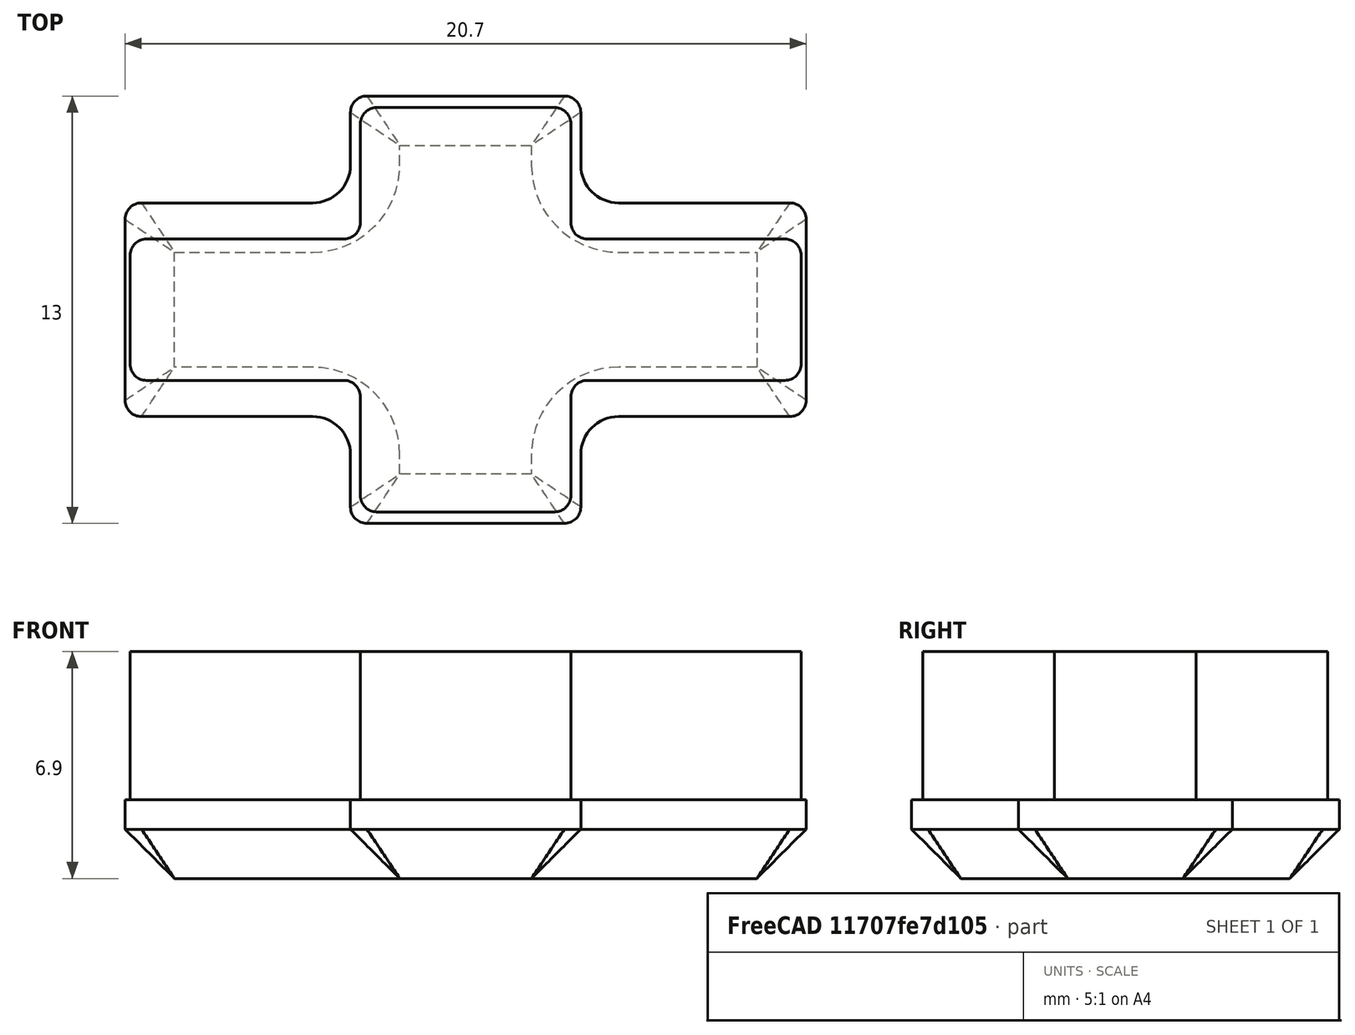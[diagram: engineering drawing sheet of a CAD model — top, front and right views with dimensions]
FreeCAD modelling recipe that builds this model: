
FCSTD DOCUMENT  (FreeCAD 0.19R24366 (Git))
Label: DPAD
License: All rights reserved
LicenseURL: http://en.wikipedia.org/wiki/All_rights_reserved
objects: Sketcher::SketchObject×2, PartDesign::Pad×2, Mesh::Feature×1, PartDesign::Chamfer×1, PartDesign::Body×1
note: 9 computed .brp shape members not serialized (recipe doc carries the construction recipe); baked Part::Feature solids carry a one-line shape summary decoded from their .brp

FEATURE [Sketcher::SketchObject] Sketch
  FullyConstrained = true
  MapMode = 5
  Support = -> [XY_Plane]
  sketch-geometry (24):
    g0: LineSegment StartX=-9.85 StartY=3.25 StartZ=0 EndX=-4.65 EndY=3.25 EndZ=0
    g1: LineSegment StartX=-3.5 StartY=4.4 StartZ=0 EndX=-3.5 EndY=6 EndZ=0
    g2: LineSegment StartX=-3 StartY=6.5 StartZ=0 EndX=3 EndY=6.5 EndZ=0
    g3: LineSegment StartX=3.5 StartY=6 StartZ=0 EndX=3.5 EndY=4.4 EndZ=0
    g4: LineSegment StartX=4.65 StartY=3.25 StartZ=0 EndX=9.85 EndY=3.25 EndZ=0
    g5: LineSegment StartX=10.35 StartY=2.75 StartZ=0 EndX=10.35 EndY=-2.75 EndZ=0
    g6: LineSegment StartX=9.85 StartY=-3.25 StartZ=0 EndX=4.65 EndY=-3.25 EndZ=0
    g7: LineSegment StartX=3.5 StartY=-4.4 StartZ=0 EndX=3.5 EndY=-6 EndZ=0
    g8: LineSegment StartX=3 StartY=-6.5 StartZ=0 EndX=-3 EndY=-6.5 EndZ=0
    g9: LineSegment StartX=-3.5 StartY=-6 StartZ=0 EndX=-3.5 EndY=-4.4 EndZ=0
    g10: LineSegment StartX=-4.65 StartY=-3.25 StartZ=0 EndX=-9.85 EndY=-3.25 EndZ=0
    g11: LineSegment StartX=-10.35 StartY=-2.75 StartZ=0 EndX=-10.35 EndY=2.75 EndZ=0
    g12: ArcOfCircle CenterX=-9.85 CenterY=2.75 CenterZ=0 NormalX=0 NormalY=0 NormalZ=1 AngleXU=0 Radius=0.5 StartAngle=1.5708 EndAngle=3.14159
    g13: ArcOfCircle CenterX=-3 CenterY=6 CenterZ=0 NormalX=0 NormalY=0 NormalZ=1 AngleXU=0 Radius=0.5 StartAngle=1.5708 EndAngle=3.14159
    g14: ArcOfCircle CenterX=3 CenterY=6 CenterZ=0 NormalX=0 NormalY=0 NormalZ=1 AngleXU=0 Radius=0.5 StartAngle=6e-16 EndAngle=1.5708
    g15: ArcOfCircle CenterX=9.85 CenterY=2.75 CenterZ=0 NormalX=0 NormalY=0 NormalZ=1 AngleXU=0 Radius=0.5 StartAngle=0 EndAngle=1.5708
    g16: ArcOfCircle CenterX=9.85 CenterY=-2.75 CenterZ=0 NormalX=0 NormalY=0 NormalZ=1 AngleXU=0 Radius=0.5 StartAngle=4.71239 EndAngle=6.28319
    g17: ArcOfCircle CenterX=3 CenterY=-6 CenterZ=0 NormalX=0 NormalY=0 NormalZ=1 AngleXU=0 Radius=0.5 StartAngle=4.71239 EndAngle=6.28319
    g18: ArcOfCircle CenterX=-3 CenterY=-6 CenterZ=0 NormalX=0 NormalY=0 NormalZ=1 AngleXU=0 Radius=0.5 StartAngle=3.14159 EndAngle=4.71239
    g19: ArcOfCircle CenterX=-9.85 CenterY=-2.75 CenterZ=0 NormalX=0 NormalY=0 NormalZ=1 AngleXU=0 Radius=0.5 StartAngle=3.14159 EndAngle=4.71239
    g20: ArcOfCircle CenterX=-4.65 CenterY=-4.4 CenterZ=0 NormalX=0 NormalY=0 NormalZ=1 AngleXU=0 Radius=1.15 StartAngle=2e-16 EndAngle=1.5708
    g21: ArcOfCircle CenterX=4.65 CenterY=-4.4 CenterZ=0 NormalX=0 NormalY=0 NormalZ=1 AngleXU=0 Radius=1.15 StartAngle=1.5708 EndAngle=3.14159
    g22: ArcOfCircle CenterX=4.65 CenterY=4.4 CenterZ=0 NormalX=0 NormalY=0 NormalZ=1 AngleXU=0 Radius=1.15 StartAngle=3.14159 EndAngle=4.71239
    g23: ArcOfCircle CenterX=-4.65 CenterY=4.4 CenterZ=0 NormalX=0 NormalY=0 NormalZ=1 AngleXU=0 Radius=1.15 StartAngle=4.71239 EndAngle=6.28319
  constraints (56):
    c: Horizontal(g2)
    c: Vertical(g3)
    c: Horizontal(g4)
    c: Vertical(g5)
    c: Horizontal(g6)
    c: Vertical(g7)
    c: Horizontal(g8)
    c: Vertical(g9)
    c: Horizontal(g10)
    c: Tangent(g11,g12) = 1.5708
    c: Tangent(g0,g12) = 1.5708
    c: Tangent(g1,g13) = 1.5708
    c: Tangent(g2,g13) = 1.5708
    c: Tangent(g2,g14) = 1.5708
    c: Tangent(g3,g14) = 1.5708
    c: Tangent(g4,g15) = 1.5708
    c: Tangent(g5,g15) = 1.5708
    c: Tangent(g5,g16) = 1.5708
    c: Tangent(g6,g16) = 1.5708
    c: Tangent(g8,g17) = 1.5708
    c: Tangent(g7,g17) = 1.5708
    c: Tangent(g9,g18) = 1.5708
    c: Tangent(g8,g18) = 1.5708
    c: Tangent(g11,g19) = 1.5708
    c: Tangent(g10,g19) = 1.5708
    c: Tangent(g10,g20) = -1.5708
    c: Tangent(g9,g20) = -1.5708
    c: Tangent(g7,g21) = -1.5708
    c: Tangent(g6,g21) = -1.5708
    c: Tangent(g3,g22) = -1.5708
    c: Tangent(g4,g22) = -1.5708
    c: Tangent(g0,g23) = -1.5708
    c: Tangent(g1,g23) = -1.5708
    c: Vertical(g11)
    c: Horizontal(g0)
    c: Equal(g8,g2)
    c: Equal(g5,g11)
    c: Equal(g12,g19)
    c: Equal(g19,g15)
    c: Equal(g16,g17)
    c: Equal(g17,g18)
    c: Vertical(g1)
    c: Symmetric(g6,g4,g-1)
    c: Symmetric(g13,g14,g-2)
    c: Equal(g21,g22)
    c: Equal(g22,g23)
    c: Equal(g23,g20)
    c: DistanceY(g6,g4) = 6.5
    c: DistanceX(g8,g8) = 6
    c: Symmetric(g13,g18,g-1)
    c: Symmetric(g15,g12,g-2)
    c: Radius(g20) = 1.15
    c: Radius(g16) = 0.5
    c: Equal(g12,g13)
    c: DistanceX(g0,g0) = 5.2
    c: DistanceY(g8,g2) = 13
FEATURE [PartDesign::Pad] Pad
  Direction = (1,1,1)
  Length = 2.4
  Length2 = 100
  Profile = -> Sketch
  Type = 0
FEATURE [Sketcher::SketchObject] Sketch001
  FullyConstrained = true
  MapMode = 5
  Placement = pos=(0,0,2.4) rot=(0,0,1;0rad)
  Support = -> [Pad]
  sketch-geometry (24):
    g0: LineSegment StartX=-9.7 StartY=2.15 StartZ=0 EndX=-3.7 EndY=2.15 EndZ=0
    g1: LineSegment StartX=-3.2 StartY=2.65 StartZ=0 EndX=-3.2 EndY=5.65 EndZ=0
    g2: LineSegment StartX=-2.7 StartY=6.15 StartZ=0 EndX=2.7 EndY=6.15 EndZ=0
    g3: LineSegment StartX=3.2 StartY=5.65 StartZ=0 EndX=3.2 EndY=2.65 EndZ=0
    g4: LineSegment StartX=3.7 StartY=2.15 StartZ=0 EndX=9.7 EndY=2.15 EndZ=0
    g5: LineSegment StartX=10.2 StartY=1.65 StartZ=0 EndX=10.2 EndY=-1.65 EndZ=0
    g6: LineSegment StartX=9.7 StartY=-2.15 StartZ=0 EndX=3.7 EndY=-2.15 EndZ=0
    g7: LineSegment StartX=3.2 StartY=-2.65 StartZ=0 EndX=3.2 EndY=-5.65 EndZ=0
    g8: LineSegment StartX=2.7 StartY=-6.15 StartZ=0 EndX=-2.7 EndY=-6.15 EndZ=0
    g9: LineSegment StartX=-3.2 StartY=-5.65 StartZ=0 EndX=-3.2 EndY=-2.65 EndZ=0
    g10: LineSegment StartX=-3.7 StartY=-2.15 StartZ=0 EndX=-9.7 EndY=-2.15 EndZ=0
    g11: LineSegment StartX=-10.2 StartY=-1.65 StartZ=0 EndX=-10.2 EndY=1.65 EndZ=0
    g12: ArcOfCircle CenterX=-2.7 CenterY=5.65 CenterZ=0 NormalX=0 NormalY=0 NormalZ=1 AngleXU=0 Radius=0.5 StartAngle=1.5708 EndAngle=3.14159
    g13: ArcOfCircle CenterX=2.7 CenterY=5.65 CenterZ=0 NormalX=0 NormalY=0 NormalZ=1 AngleXU=0 Radius=0.5 StartAngle=0 EndAngle=1.5708
    g14: ArcOfCircle CenterX=9.7 CenterY=1.65 CenterZ=0 NormalX=0 NormalY=0 NormalZ=1 AngleXU=0 Radius=0.5 StartAngle=0 EndAngle=1.5708
    g15: ArcOfCircle CenterX=9.7 CenterY=-1.65 CenterZ=0 NormalX=0 NormalY=0 NormalZ=1 AngleXU=0 Radius=0.5 StartAngle=4.71239 EndAngle=6.28319
    g16: ArcOfCircle CenterX=2.7 CenterY=-5.65 CenterZ=0 NormalX=0 NormalY=0 NormalZ=1 AngleXU=0 Radius=0.5 StartAngle=4.71239 EndAngle=6.28319
    g17: ArcOfCircle CenterX=-2.7 CenterY=-5.65 CenterZ=0 NormalX=0 NormalY=0 NormalZ=1 AngleXU=0 Radius=0.5 StartAngle=3.14159 EndAngle=4.71239
    g18: ArcOfCircle CenterX=-9.7 CenterY=-1.65 CenterZ=0 NormalX=0 NormalY=0 NormalZ=1 AngleXU=0 Radius=0.5 StartAngle=3.14159 EndAngle=4.71239
    g19: ArcOfCircle CenterX=-9.7 CenterY=1.65 CenterZ=0 NormalX=0 NormalY=0 NormalZ=1 AngleXU=0 Radius=0.5 StartAngle=1.5708 EndAngle=3.14159
    g20: ArcOfCircle CenterX=-3.7 CenterY=2.65 CenterZ=0 NormalX=0 NormalY=0 NormalZ=1 AngleXU=0 Radius=0.5 StartAngle=4.71239 EndAngle=6.28319
    g21: ArcOfCircle CenterX=-3.7 CenterY=-2.65 CenterZ=0 NormalX=0 NormalY=0 NormalZ=1 AngleXU=0 Radius=0.5 StartAngle=0 EndAngle=1.5708
    g22: ArcOfCircle CenterX=3.7 CenterY=-2.65 CenterZ=0 NormalX=0 NormalY=0 NormalZ=1 AngleXU=0 Radius=0.5 StartAngle=1.5708 EndAngle=3.14159
    g23: ArcOfCircle CenterX=3.7 CenterY=2.65 CenterZ=0 NormalX=0 NormalY=0 NormalZ=1 AngleXU=0 Radius=0.5 StartAngle=3.14159 EndAngle=4.71239
  constraints (57):
    c: Horizontal(g0)
    c: Horizontal(g8)
    c: Tangent(g1,g12) = 1.5708
    c: Tangent(g2,g12) = 1.5708
    c: Tangent(g2,g13) = 1.5708
    c: Tangent(g3,g13) = 1.5708
    c: Tangent(g4,g14) = 1.5708
    c: Tangent(g5,g14) = 1.5708
    c: Tangent(g5,g15) = 1.5708
    c: Tangent(g6,g15) = 1.5708
    c: Tangent(g7,g16) = 1.5708
    c: Tangent(g8,g16) = 1.5708
    c: Tangent(g9,g17) = 1.5708
    c: Tangent(g8,g17) = 1.5708
    c: Tangent(g11,g18) = 1.5708
    c: Tangent(g10,g18) = 1.5708
    c: Tangent(g11,g19) = 1.5708
    c: Tangent(g0,g19) = 1.5708
    c: Equal(g13,g12)
    c: Equal(g12,g19)
    c: Equal(g19,g18)
    c: Equal(g18,g17)
    c: Equal(g17,g16)
    c: Equal(g16,g15)
    c: Equal(g15,g14)
    c: Tangent(g0,g20) = -1.5708
    c: Tangent(g1,g20) = -1.5708
    c: Tangent(g10,g21) = -1.5708
    c: Tangent(g9,g21) = -1.5708
    c: Tangent(g7,g22) = -1.5708
    c: Tangent(g6,g22) = -1.5708
    c: Tangent(g3,g23) = -1.5708
    c: Tangent(g4,g23) = -1.5708
    c: Horizontal(g4)
    c: Vertical(g3)
    c: Vertical(g1)
    c: Horizontal(g10)
    c: Vertical(g9)
    c: Vertical(g7)
    c: Vertical(g5)
    c: Equal(g8,g2)
    c: Equal(g11,g5)
    c: Horizontal(g6)
    c: Radius(g16) = 0.5
    c: Radius(g22) = 0.5
    c: Symmetric(g11,g11,g-1)
    c: DistanceY(g10,g0) = 4.3
    c: Symmetric(g12,g13,g-2)
    c: Equal(g20,g21)
    c: Equal(g21,g22)
    c: Equal(g22,g23)
    c: Symmetric(g17,g12,g-1)
    c: DistanceX(g11,g1) = 7
    c: Equal(g0,g4)
    c: Horizontal(g20,g23)
    c: DistanceY(g4,g2) = 4
    c: DistanceX(g1,g3) = 6.4
FEATURE [PartDesign::Pad] Pad001
  BaseFeature = -> Pad
  Direction = (1,1,1)
  Length = 4.5
  Length2 = 100
  Profile = -> Sketch001
  Type = 0
FEATURE [Mesh::Feature] GameNugg_DPad  label="GameNugg-DPad"
FEATURE [PartDesign::Chamfer] Chamfer
  Angle = 45
  Base = -> Pad001 [Face4]
  BaseFeature = -> Pad001
  ChamferType = 2
  FlipDirection = false
  Size = 1.5
  Size2 = 1
  SupportTransform = false
FEATURE [PartDesign::Body] Body
  Group = -> [Sketch,Pad,Sketch001,Pad001,Chamfer]
  Origin = -> Origin
  Tip = -> Chamfer
